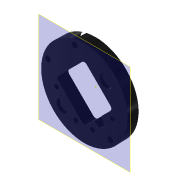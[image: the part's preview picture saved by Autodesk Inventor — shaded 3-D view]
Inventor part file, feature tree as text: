
AUTODESK INVENTOR PART (.ipt)
format: ipt  version: 2022 (Build 260153000, 153)  size: 249,856 bytes
history: native  units: in
note: dims shown in document units (in); Inventor stores cm internally (conversion verified against a paired STEP export)
features: reference x9, other x7, sketch x5, extrude x3, plane x1, hole x1, fillet x1, projected_geometry x1
ambient origin geometry x8: Origin, YZ Plane, XZ Plane, XY Plane, X Axis, Y Axis, Z Axis, Center Point
bodies: Solid1 (feature_tree)
feature tree (28):
  plane  "Work Plane1"
  extrude  "Extrusion1"  Depth=0.1575in
  hole  "Bohrung1"  [1 undecoded]
  fillet  "Rundung1"  Radius=0.9843in
  extrude  "Extrusion4"  Depth=0.0787in
  extrude  "Extrusion5"  Depth=0.0787in
  sketch  "Skizze8"  dims[d23=0.1102in d24=0.1102in d25=0.1575in d26=0.1575in d27=0.1575in d28=0.0014in d29=0.0069in d30=0.0787in d31=0.0in d32=2.126in d33=0.1102in d34=0.1102in]
  sketch  "Sketch1"  dims[d0=0.2756in d1=-0.0069in]
  reference  "Reference1"
  reference  "Reference5"
  reference  "Reference6"
  reference  "Reference7"
  sketch  "Skizze4"  dims[d9=0.1417in d10=0.75in d11=0.2559in d12=0.1575in d13=0.5635in d14=1.0in d15=0.8108in d17=0.9843in]
  reference  "Referenz9"
  reference  "Referenz10"
  reference  "Referenz11"
  reference  "Referenz12"
  reference  "Referenz13"
  sketch  "Skizze6"  dims[d18=0.9843in d19=45.0deg d20=0.9843in]
  projected_geometry  "Projizierte Kontur1"
  sketch  "Skizze7"  dims[d21=0.0787in d22=0.0787in]
  other  "<userpath>\Documents\Matchboxscope\INVENTOR\Matchboxscope_v1.iam"
  other  "Matchboxscope_v1.iam"
  other  "Matchboxscope_middle2_v1:1"
  other  "Matchboxscope_VCM_v1.iam"
  other  "Matchboxscope_middle2_m12VCMLens_v2:1"
  other  "Assembly_Matchboxscope_injectionmolded.iam"
  other  "IM_Matchboxscope_base:1"
note: 1 required parameter value undecoded (feature->parameter linkage not recoverable at this tier; creation-order binding heuristic only, values carry confidence <= 0.55)
